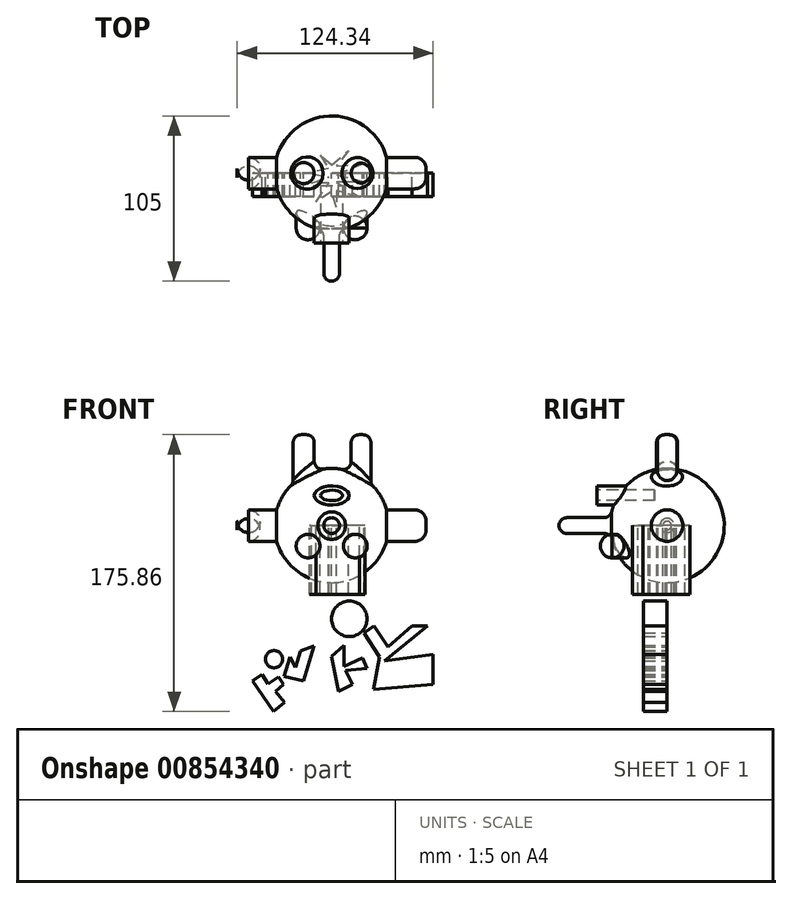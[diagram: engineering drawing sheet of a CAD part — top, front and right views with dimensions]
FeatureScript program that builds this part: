
annotation { "Feature Type Name" : "Feature", "Feature Type Description" : "" }
export const myFeature = defineFeature(function(context is Context, id is Id, definition is map)
    precondition{}
    {
        {
            var Q0;
            Q0=qCreatedBy(makeId("Front.planeOp"),FACE);
            var sketch = newSketch(context, id + "F0", { "sketchPlane" : qUnion([Q0])});
            skCircle(sketch, "E0", {"center": v(0, 0) * mm, "radius": 36.3 * mm});
            skLineSegment(sketch, "E1", {"start": v(0, 36.3) * mm, "end": v(0, -36.3) * mm});
            skSolve(sketch);
        }
        {
            var Q0;
            {var subQ0=sQuery(id+"F0.wireOp",EDGE,"E1");Q0=makeQuery(id+"F0.imprint","IMPRINT",FACE,{"disambiguationData":[TD([[makeQuery(id+"F0.imprint","IMPRINT",EDGE,{"derivedFrom":subQ0}),-1.0]])]});}
            var Q1;
            Q1=sQuery(id+"F0.wireOp",EDGE,"E1");
            revolve(context, id + "F1", {"surfaceOperationType" : NewSurfaceOperationType.NEW, "entities" : qUnion([Q0]), "axis" : qUnion([Q1]), "revolveType" : RevolveType.FULL});
        }
        {
            var Q0;
            Q0=qCreatedBy(makeId("Top.planeOp"),FACE);
            var sketch = newSketch(context, id + "F2", { "sketchPlane" : qUnion([Q0])});
            skCircle(sketch, "E2", {"center": v(18.64, 0) * mm, "radius": 6.26 * mm});
            skCircle(sketch, "E3", {"center": v(-17.77, 0) * mm, "radius": 6.7 * mm});
            skSolve(sketch);
        }
        {
            var Q0;
            Q0 = qSketchRegion(id + "F2", true);
            extrude(context, id + "F3", {"entities" : qUnion([Q0]), "operationType" : NewBodyOperationType.ADD, "depth" : 57.7 * mm, "offsetDistance" : 25 * mm});
        }
        {
            var Q0;
            Q0=makeQuery(id+"F3.opExtrude","CAP_FACE",FACE,{"disambiguationData":[OSD([sQuery(id+"F2.wireOp",EDGE,"E2")])],"isStart":false});
            var Q1;
            Q1=makeQuery(id+"F3.opExtrude","CAP_EDGE",EDGE,{"disambiguationData":[OSD([sQuery(id+"F2.wireOp",EDGE,"E3")])],"isStart":false});
            var Q2;
            Q2=makeQuery(id+"F3.opExtrude","SWEPT_FACE",FACE,{"disambiguationData":[OSD([sQuery(id+"F2.wireOp",EDGE,"E3")])]});
            var Q3;
            Q3=makeQuery(id+"F3.opExtrude","SWEPT_FACE",FACE,{"disambiguationData":[OSD([sQuery(id+"F2.wireOp",EDGE,"E2")])]});
            fillet(context, id + "F4", {"entities" : qUnion([Q0, Q1, Q2, Q3]), "radius" : 5 * mm, "tangentPropagation" : true, "allowEdgeOverflow" : false});
        }
        {
            var Q0;
            Q0=qCreatedBy(makeId("Right.planeOp"),FACE);
            var sketch = newSketch(context, id + "F5", { "sketchPlane" : qUnion([Q0])});
            skCircle(sketch, "E4", {"center": v(0, 0) * mm, "radius": 10 * mm});
            skSolve(sketch);
        }
        {
            var Q0;
            Q0 = qSketchRegion(id + "F5", true);
            extrude(context, id + "F6", {"entities" : qUnion([Q0]), "operationType" : NewBodyOperationType.ADD, "depth" : 60 * mm, "offsetDistance" : 25 * mm, "hasSecondDirection" : true, "secondDirectionOppositeDirection" : true, "secondDirectionDepth" : 60 * mm});
        }
        {
            var Q0;
            Q0=makeQuery(id+"F6.opExtrude","CAP_FACE",FACE,{"disambiguationData":[OSD([sQuery(id+"F5.wireOp",EDGE,"E4")])],"isStart":false});
            var Q1;
            Q1=makeQuery(id+"F6.opExtrude","CAP_FACE",FACE,{"disambiguationData":[OSD([sQuery(id+"F5.wireOp",EDGE,"E4")])],"isStart":true});
            fillet(context, id + "F7", {"entities" : qUnion([Q0, Q1]), "radius" : 7.24 * mm, "tangentPropagation" : true, "allowEdgeOverflow" : false});
        }
        {
            var Q0;
            Q0=qCreatedBy(makeId("Front.planeOp"),FACE);
            var sketch = newSketch(context, id + "F8", { "sketchPlane" : qUnion([Q0])});
            skLineSegment(sketch, "E5", {"start": v(0, 0) * mm, "end": v(-15, 0) * mm});
            skLineSegment(sketch, "E6", {"start": v(-15, 0) * mm, "end": v(15, 0) * mm});
            skLineSegment(sketch, "E7", {"start": v(15, 0) * mm, "end": v(15, -13) * mm});
            skLineSegment(sketch, "E8", {"start": v(-15, 0) * mm, "end": v(-15, -13) * mm});
            skCircle(sketch, "E9", {"center": v(15, -13) * mm, "radius": 7.5 * mm});
            skCircle(sketch, "E10", {"center": v(-15, -13) * mm, "radius": 7.5 * mm});
            skSolve(sketch);
        }
        {
            var Q0;
            Q0 = qSketchRegion(id + "F8", true);
            extrude(context, id + "F9", {"entities" : qUnion([Q0]), "operationType" : NewBodyOperationType.ADD, "depth" : 34.9 * mm, "offsetDistance" : 25 * mm});
        }
        {
            var Q0;
            Q0=makeQuery(id+"F9.opExtrude","CAP_FACE",FACE,{"disambiguationData":[OSD([sQuery(id+"F8.wireOp",EDGE,"E9")])],"isStart":false});
            var sketch = newSketch(context, id + "F10", { "sketchPlane" : qUnion([Q0])});
            skCircle(sketch, "E11.0.0", {"center": v(15, -13) * mm, "radius": 7.5 * mm});
            skCircle(sketch, "E12.0", {"center": v(-15, -13) * mm, "radius": 7.5 * mm});
            skLineSegment(sketch, "E13", {"start": v(15, -13) * mm, "end": v(15, -20.5) * mm});
            skLineSegment(sketch, "E14", {"start": v(15, -20.5) * mm, "end": v(15, -5.5) * mm});
            skLineSegment(sketch, "E15", {"start": v(-15, -13) * mm, "end": v(-15, -20.5) * mm});
            skLineSegment(sketch, "E16", {"start": v(-15, -20.5) * mm, "end": v(-15, -5.5) * mm});
            skSolve(sketch);
        }
        {
            var Q0;
            {var subQ0=sQuery(id+"F10.wireOp",EDGE,"E14");var subQ4=makeQuery(id+"F10.imprint","IMPRINT",VERTEX,{"derivedFrom":subQ0});Q0=makeQuery(id+"F10.imprint","IMPRINT",FACE,{"disambiguationData":[TD([[makeQuery(id+"F10.imprint","IMPRINT",EDGE,{"disambiguationData":[TD([[subQ4,1.0]])],"derivedFrom":subQ0}),-1.0]])]});}
            var Q1;
            Q1=sQuery(id+"F10.wireOp",EDGE,"E14");
            revolve(context, id + "F11", {"surfaceOperationType" : NewSurfaceOperationType.NEW, "entities" : qUnion([Q0]), "axis" : qUnion([Q1]), "revolveType" : RevolveType.FULL});
        }
        {
            var Q0;
            Q0=makeQuery(id+"F9.opExtrude","CAP_FACE",FACE,{"disambiguationData":[OSD([sQuery(id+"F8.wireOp",EDGE,"E10")])],"isStart":false});
            var sketch = newSketch(context, id + "F12", { "sketchPlane" : qUnion([Q0])});
            skCircle(sketch, "E17.0.0", {"center": v(-15, -13) * mm, "radius": 7.5 * mm});
            skLineSegment(sketch, "E18", {"start": v(-15, -13) * mm, "end": v(-15, -20.5) * mm});
            skLineSegment(sketch, "E19", {"start": v(-15, -20.5) * mm, "end": v(-15, -5.5) * mm});
            skSolve(sketch);
        }
        {
            var Q0;
            {var subQ0=sQuery(id+"F12.wireOp",EDGE,"E19");var subQ4=makeQuery(id+"F12.imprint","IMPRINT",VERTEX,{"derivedFrom":subQ0});Q0=makeQuery(id+"F12.imprint","IMPRINT",FACE,{"disambiguationData":[TD([[makeQuery(id+"F12.imprint","IMPRINT",EDGE,{"disambiguationData":[TD([[subQ4,1.0]])],"derivedFrom":subQ0}),-1.0]])]});}
            var Q1;
            Q1=sQuery(id+"F12.wireOp",EDGE,"E19");
            revolve(context, id + "F13", {"operationType" : NewBodyOperationType.ADD, "surfaceOperationType" : NewSurfaceOperationType.NEW, "entities" : qUnion([Q0]), "axis" : qUnion([Q1]), "revolveType" : RevolveType.FULL});
        }
        {
            var Q0;
            Q0=qCreatedBy(makeId("Front.planeOp"),FACE);
            var sketch = newSketch(context, id + "F14", { "sketchPlane" : qUnion([Q0])});
            skCircle(sketch, "E20", {"center": v(0, 0) * mm, "radius": 5 * mm});
            skSolve(sketch);
        }
        {
            var Q0;
            Q0 = qSketchRegion(id + "F14", true);
            extrude(context, id + "F15", {"entities" : qUnion([Q0]), "operationType" : NewBodyOperationType.ADD, "depth" : 63.7 * mm, "offsetDistance" : 25 * mm});
        }
        {
            var Q0;
            Q0=makeQuery(id+"F15.opExtrude","CAP_FACE",FACE,{"disambiguationData":[OSD([sQuery(id+"F14.wireOp",EDGE,"E20")])],"isStart":false});
            var sketch = newSketch(context, id + "F16", { "sketchPlane" : qUnion([Q0])});
            skCircle(sketch, "E21.0.0", {"center": v(0, 0) * mm, "radius": 5 * mm});
            skLineSegment(sketch, "E22", {"start": v(0, -5) * mm, "end": v(0, 5) * mm});
            skSolve(sketch);
        }
        {
            var Q0;
            {var subQ0=sQuery(id+"F16.wireOp",EDGE,"E22");Q0=makeQuery(id+"F16.imprint","IMPRINT",FACE,{"disambiguationData":[TD([[makeQuery(id+"F16.imprint","IMPRINT",EDGE,{"derivedFrom":subQ0}),-1.0]])]});}
            var Q1;
            Q1=sQuery(id+"F16.wireOp",EDGE,"E22");
            revolve(context, id + "F17", {"operationType" : NewBodyOperationType.ADD, "surfaceOperationType" : NewSurfaceOperationType.NEW, "entities" : qUnion([Q0]), "axis" : qUnion([Q1]), "revolveType" : RevolveType.FULL});
        }
        {
            var Q0;
            Q0=makeQuery(id+"F15.opExtrude","SWEPT_FACE",FACE,{"disambiguationData":[OSD([sQuery(id+"F14.wireOp",EDGE,"E20")])]});
            fillet(context, id + "F18", {"entities" : qUnion([Q0]), "radius" : 5 * mm, "tangentPropagation" : true, "allowEdgeOverflow" : false});
        }
        {
            var Q0;
            Q0=qCreatedBy(makeId("Front.planeOp"),FACE);
            var sketch = newSketch(context, id + "F19", { "sketchPlane" : qUnion([Q0])});
            skEllipse(sketch, "E23", {"center": v(0, 19.14) * mm, "majorRadius": 11.06 * mm, "minorRadius": 6.06 * mm, "majorAxis": v(-1, 0)});
            skSolve(sketch);
        }
        {
            var Q0;
            Q0 = qSketchRegion(id + "F19", true);
            extrude(context, id + "F20", {"entities" : qUnion([Q0]), "operationType" : NewBodyOperationType.ADD, "depth" : 44.4 * mm, "offsetDistance" : 25 * mm});
        }
        {
            var Q0;
            Q0=makeQuery(id+"F20.opExtrude","CAP_FACE",FACE,{"disambiguationData":[OSD([sQuery(id+"F19.wireOp",EDGE,"E23")])],"isStart":false});
            var sketch = newSketch(context, id + "F21", { "sketchPlane" : qUnion([Q0])});
            skEllipse(sketch, "E24", {"center": v(0, 19.14) * mm, "majorRadius": 6.98 * mm, "minorRadius": 3.34 * mm, "majorAxis": v(-1, 0)});
            skSolve(sketch);
        }
        {
            var Q0;
            Q0 = qSketchRegion(id + "F21", true);
            extrude(context, id + "F22", {"entities" : qUnion([Q0]), "operationType" : NewBodyOperationType.REMOVE, "oppositeDirection" : true, "depth" : 36.5 * mm, "offsetDistance" : 25 * mm});
        }
        {
            var Q0;
            Q0=qCreatedBy(makeId("Top.planeOp"),FACE);
            var sketch = newSketch(context, id + "F23", { "sketchPlane" : qUnion([Q0])});
            skLineSegment(sketch, "E25", {"start": v(0, 5.06) * mm, "end": v(10.79, 14.37) * mm});
            skLineSegment(sketch, "E26", {"start": v(10.79, 14.37) * mm, "end": v(2.92, 4.44) * mm});
            skLineSegment(sketch, "E27", {"start": v(2.92, 4.44) * mm, "end": v(20.52, 6) * mm});
            skLineSegment(sketch, "E28", {"start": v(20.52, 6) * mm, "end": v(2.92, -1.05) * mm});
            skLineSegment(sketch, "E29", {"start": v(2.92, -1.05) * mm, "end": v(21.13, -5.75) * mm});
            skLineSegment(sketch, "E30", {"start": v(21.13, -5.75) * mm, "end": v(2.92, -5.75) * mm});
            skLineSegment(sketch, "E31", {"start": v(2.92, -5.75) * mm, "end": v(17.74, -15.25) * mm});
            skLineSegment(sketch, "E32", {"start": v(17.74, -15.25) * mm, "end": v(2.92, -11.05) * mm});
            skLineSegment(sketch, "E33", {"start": v(2.92, -11.05) * mm, "end": v(2.92, -21.98) * mm});
            skLineSegment(sketch, "E34", {"start": v(2.92, -21.98) * mm, "end": v(0, -11.74) * mm});
            skLineSegment(sketch, "E35", {"start": v(0, -11.74) * mm, "end": v(-9.9, -18.37) * mm});
            skLineSegment(sketch, "E36", {"start": v(-9.9, -18.37) * mm, "end": v(-1.82, -6.35) * mm});
            skLineSegment(sketch, "E37", {"start": v(-1.82, -6.35) * mm, "end": v(-12.71, -6.35) * mm});
            skLineSegment(sketch, "E38", {"start": v(-12.71, -6.35) * mm, "end": v(-1.76, -2.63) * mm});
            skLineSegment(sketch, "E39", {"start": v(0, 5.06) * mm, "end": v(-7.41, 11.35) * mm});
            skLineSegment(sketch, "E40", {"start": v(-7.41, 11.35) * mm, "end": v(-1.94, 2.89) * mm});
            skLineSegment(sketch, "E41", {"start": v(-1.94, 2.89) * mm, "end": v(-13.96, 0) * mm});
            skLineSegment(sketch, "E42", {"start": v(-13.96, 0) * mm, "end": v(-1.76, -2.63) * mm});
            skSolve(sketch);
        }
        {
            var Q0;
            Q0 = qSketchRegion(id + "F23", true);
            extrude(context, id + "F24", {"entities" : qUnion([Q0]), "oppositeDirection" : true, "depth" : 43.6 * mm, "offsetDistance" : 25 * mm});
        }
        {
            var Q0;
            Q0=qCreatedBy(makeId("Front.planeOp"),FACE);
            var sketch = newSketch(context, id + "F25", { "sketchPlane" : qUnion([Q0])});
            skLineSegment(sketch, "E43", {"start": v(64.34, -101) * mm, "end": v(64.34, -81.96) * mm});
            skLineSegment(sketch, "E44", {"start": v(64.34, -81.96) * mm, "end": v(33.65, -86.12) * mm});
            skLineSegment(sketch, "E45", {"start": v(33.65, -86.12) * mm, "end": v(60.85, -63.68) * mm});
            skLineSegment(sketch, "E46", {"start": v(60.85, -63.68) * mm, "end": v(51.1, -63.68) * mm});
            skLineSegment(sketch, "E47", {"start": v(51.1, -63.68) * mm, "end": v(35.8, -76.93) * mm});
            skLineSegment(sketch, "E48", {"start": v(35.8, -76.93) * mm, "end": v(27.03, -63.68) * mm});
            skLineSegment(sketch, "E49", {"start": v(27.03, -63.68) * mm, "end": v(20.4, -68.07) * mm});
            skLineSegment(sketch, "E50", {"start": v(20.4, -68.07) * mm, "end": v(30.48, -83.3) * mm});
            skLineSegment(sketch, "E51", {"start": v(30.48, -83.3) * mm, "end": v(26.47, -104.1) * mm});
            skLineSegment(sketch, "E52", {"start": v(26.47, -104.1) * mm, "end": v(64.34, -101) * mm});
            skLineSegment(sketch, "E53", {"start": v(22.57, -90.7) * mm, "end": v(19.55, -84.09) * mm});
            skLineSegment(sketch, "E54", {"start": v(19.55, -84.09) * mm, "end": v(7.7, -89.5) * mm});
            skLineSegment(sketch, "E55", {"start": v(7.7, -89.5) * mm, "end": v(7.7, -76.29) * mm});
            skLineSegment(sketch, "E56", {"start": v(7.7, -76.29) * mm, "end": v(0, -83.27) * mm});
            skLineSegment(sketch, "E57", {"start": v(0, -83.27) * mm, "end": v(4.32, -105.37) * mm});
            skLineSegment(sketch, "E58", {"start": v(4.32, -105.37) * mm, "end": v(13.18, -101) * mm});
            skLineSegment(sketch, "E59", {"start": v(13.18, -101) * mm, "end": v(8.7, -91.91) * mm});
            skLineSegment(sketch, "E60", {"start": v(8.7, -91.91) * mm, "end": v(22.57, -90.7) * mm});
            skCircle(sketch, "E61", {"center": v(11.24, -59.22) * mm, "radius": 11.27 * mm});
            skLineSegment(sketch, "E62", {"start": v(-18, -98.63) * mm, "end": v(-11.28, -76.36) * mm});
            skLineSegment(sketch, "E63", {"start": v(-11.28, -76.36) * mm, "end": v(-19.71, -79.63) * mm});
            skLineSegment(sketch, "E64", {"start": v(-19.71, -79.63) * mm, "end": v(-23.09, -90.1) * mm});
            skLineSegment(sketch, "E65", {"start": v(-23.09, -90.1) * mm, "end": v(-26.4, -83.47) * mm});
            skLineSegment(sketch, "E66", {"start": v(-26.4, -83.47) * mm, "end": v(-30.34, -95.69) * mm});
            skLineSegment(sketch, "E67", {"start": v(-30.34, -95.69) * mm, "end": v(-18, -98.63) * mm});
            skLineSegment(sketch, "E68", {"start": v(-30.46, -100.94) * mm, "end": v(-35.67, -105.3) * mm});
            skLineSegment(sketch, "E69", {"start": v(-35.67, -105.3) * mm, "end": v(-29.9, -112.2) * mm});
            skLineSegment(sketch, "E70", {"start": v(-29.9, -112.2) * mm, "end": v(-37.03, -118.16) * mm});
            skLineSegment(sketch, "E71", {"start": v(-37.03, -118.16) * mm, "end": v(-50.16, -98.63) * mm});
            skLineSegment(sketch, "E72", {"start": v(-50.16, -98.63) * mm, "end": v(-44.28, -94.68) * mm});
            skLineSegment(sketch, "E73", {"start": v(-44.28, -94.68) * mm, "end": v(-40.37, -100.5) * mm});
            skLineSegment(sketch, "E74", {"start": v(-40.37, -100.5) * mm, "end": v(-33.82, -96.1) * mm});
            skLineSegment(sketch, "E75", {"start": v(-33.82, -96.1) * mm, "end": v(-30.46, -100.94) * mm});
            skCircle(sketch, "E76", {"center": v(-36.6, -84.87) * mm, "radius": 5.46 * mm});
            skPoint(sketch, "E76.centerSnap0", {"position": v(-21.4, -84.87) * mm});
            skSolve(sketch);
        }
        {
            var Q0;
            Q0 = qSketchRegion(id + "F25", true);
            extrude(context, id + "F26", {"entities" : qUnion([Q0]), "depth" : 15 * mm, "offsetDistance" : 25 * mm});
        }
    });
